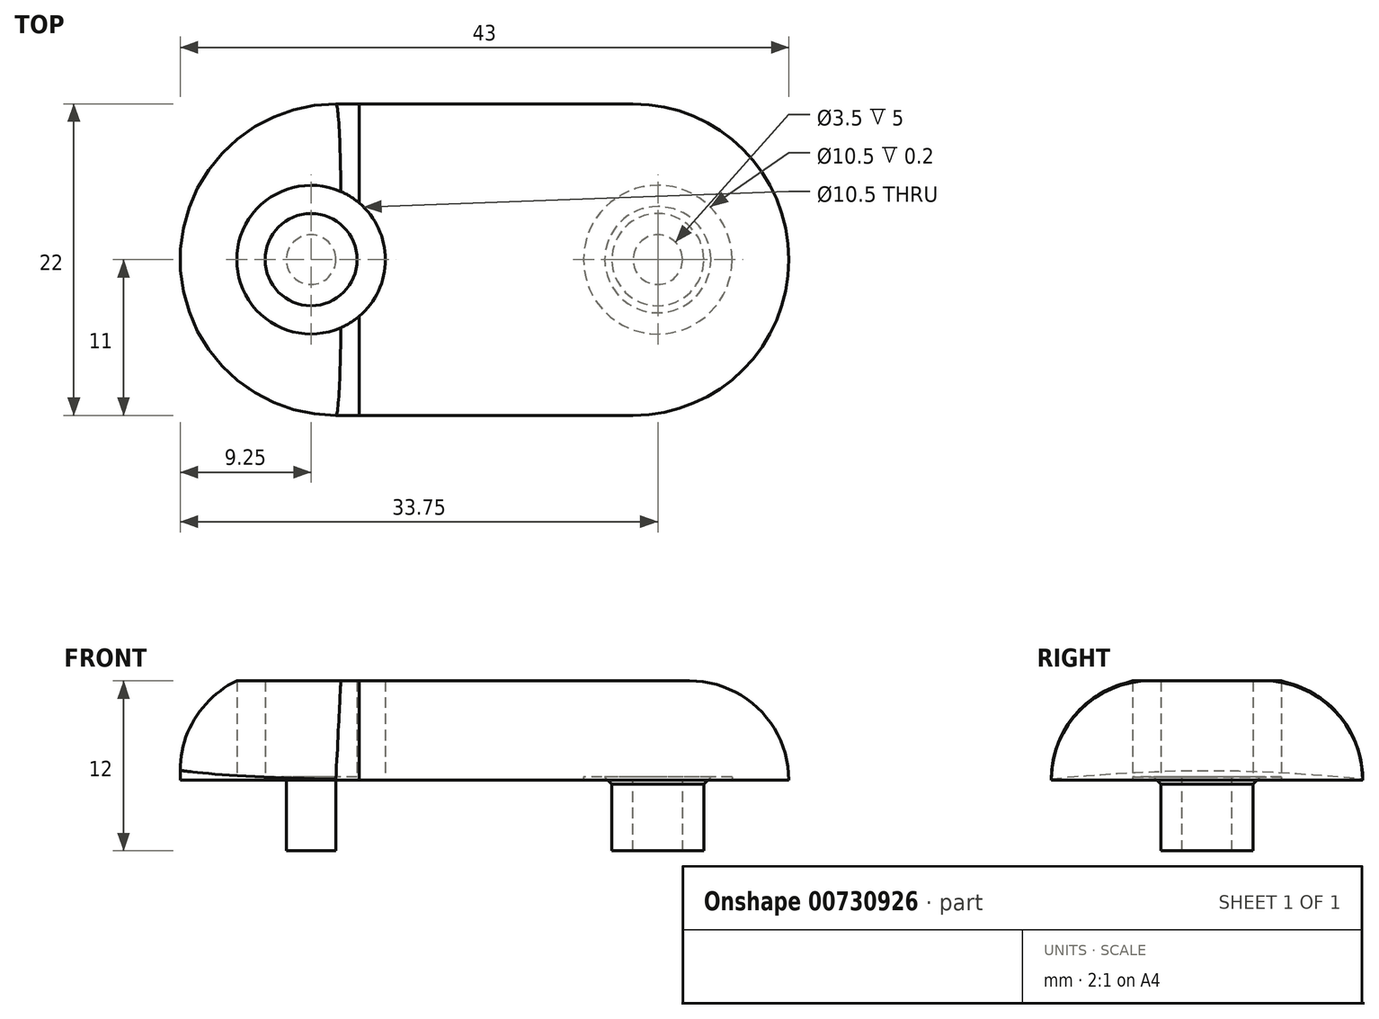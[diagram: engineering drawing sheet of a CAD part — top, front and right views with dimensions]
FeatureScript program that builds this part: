
annotation { "Feature Type Name" : "Feature", "Feature Type Description" : "" }
export const myFeature = defineFeature(function(context is Context, id is Id, definition is map)
    precondition{}
    {
        {
            var Q0;
            Q0=qCreatedBy(makeId("Top.planeOp"),FACE);
            var sketch = newSketch(context, id + "F0", { "sketchPlane" : qUnion([Q0])});
            skLineSegment(sketch, "E0", {"start": v(21.5, 0) * mm, "end": v(-21.5, 0) * mm, "construction": true});
            skLineSegment(sketch, "E1", {"start": v(0, 11) * mm, "end": v(0, -11) * mm, "construction": true});
            skLineSegment(sketch, "E2", {"start": v(-21.5, 0) * mm, "end": v(-21.5, 0) * mm});
            skLineSegment(sketch, "E3", {"start": v(-10.5, 11) * mm, "end": v(10.5, 11) * mm});
            skLineSegment(sketch, "E4", {"start": v(21.5, 0) * mm, "end": v(21.5, 0) * mm});
            skLineSegment(sketch, "E5", {"start": v(10.5, -11) * mm, "end": v(-10.5, -11) * mm});
            skPoint(sketch, "E6.visualSharp", {"position": v(-21.5, 11) * mm});
            skArc(sketch, "E6.filletArc", {"start": v(-10.5, 11) * mm, "mid": v(-18.28, 7.78) * mm, "end": v(-21.5, 0) * mm});
            skPoint(sketch, "E7.visualSharp", {"position": v(-21.5, -11) * mm});
            skArc(sketch, "E7.filletArc", {"start": v(-21.5, 0) * mm, "mid": v(-18.28, -7.78) * mm, "end": v(-10.5, -11) * mm});
            skPoint(sketch, "E8.visualSharp", {"position": v(21.5, -11) * mm});
            skArc(sketch, "E8.filletArc", {"start": v(10.5, -11) * mm, "mid": v(18.28, -7.78) * mm, "end": v(21.5, 0) * mm});
            skPoint(sketch, "E9.visualSharp", {"position": v(21.5, 11) * mm});
            skArc(sketch, "E9.filletArc", {"start": v(21.5, 0) * mm, "mid": v(18.28, 7.78) * mm, "end": v(10.5, 11) * mm});
            skCircle(sketch, "E10", {"center": v(12.25, 0) * mm, "radius": 3.25 * mm});
            skCircle(sketch, "E11.0", {"center": v(12.25, 0) * mm, "radius": 1.75 * mm});
            skCircle(sketch, "E12.MirrorC", {"center": v(-12.25, 0) * mm, "radius": 1.75 * mm});
            skCircle(sketch, "E13.MirrorC", {"center": v(-12.25, 0) * mm, "radius": 3.25 * mm});
            skCircle(sketch, "E14.0", {"center": v(12.25, 0) * mm, "radius": 5.25 * mm});
            skCircle(sketch, "E15.MirrorC", {"center": v(-12.25, 0) * mm, "radius": 5.25 * mm});
            skSolve(sketch);
        }
        {
            var Q0;
            Q0 = qSketchRegion(id + "F0", true);
            var Q1;
            Q1=makeQuery(id+"F0.imprint","IMPRINT",FACE,{"disambiguationData":[TD([[makeQuery(id+"F0.imprint","IMPRINT",EDGE,{"derivedFrom":sQuery(id+"F0.wireOp",EDGE,"E10")}),1.0]])]});
            var Q2;
            Q2=makeQuery(id+"F0.imprint","IMPRINT",FACE,{"disambiguationData":[TD([[makeQuery(id+"F0.imprint","IMPRINT",EDGE,{"derivedFrom":sQuery(id+"F0.wireOp",EDGE,"464fe94d-2eab-4d05-92af-5368927bac3c0.MirrorC")}),-1.0]])]});
            var Q3;
            Q3=makeQuery(id+"F0.imprint","IMPRINT",FACE,{"disambiguationData":[TD([[makeQuery(id+"F0.imprint","IMPRINT",EDGE,{"derivedFrom":sQuery(id+"F0.wireOp",EDGE,"E13.MirrorC")}),1.0]])]});
            var Q4;
            Q4=makeQuery(id+"F0.imprint","IMPRINT",FACE,{"disambiguationData":[TD([[makeQuery(id+"F0.imprint","IMPRINT",EDGE,{"derivedFrom":sQuery(id+"F0.wireOp",EDGE,"E12.MirrorC")}),1.0]])]});
            var Q5;
            Q5=makeQuery(id+"F0.imprint","IMPRINT",FACE,{"disambiguationData":[TD([[makeQuery(id+"F0.imprint","IMPRINT",EDGE,{"derivedFrom":sQuery(id+"F0.wireOp",EDGE,"E12.MirrorC")}),-1.0]])]});
            var Q6;
            Q6=makeQuery(id+"F0.imprint","IMPRINT",FACE,{"disambiguationData":[TD([[makeQuery(id+"F0.imprint","IMPRINT",EDGE,{"derivedFrom":sQuery(id+"F0.wireOp",EDGE,"E10")}),-1.0]])]});
            var Q7;
            Q7=makeQuery(id+"F0.imprint","IMPRINT",FACE,{"disambiguationData":[TD([[makeQuery(id+"F0.imprint","IMPRINT",EDGE,{"derivedFrom":sQuery(id+"F0.wireOp",EDGE,"E11.0")}),1.0]])]});
            extrude(context, id + "F1", {"entities" : qUnion([Q0, Q1, Q2, Q3, Q4, Q5, Q6, Q7]), "depth" : 7 * mm, "offsetDistance" : 25 * mm});
        }
        {
            var Q0;
            Q0=makeQuery(id+"F1.opExtrude","CAP_EDGE",EDGE,{"disambiguationData":[OSD([sQuery(id+"F0.wireOp",EDGE,"E3")])],"isStart":false});
            fillet(context, id + "F2", {"entities" : qUnion([Q0]), "radius" : 7 * mm, "tangentPropagation" : true, "allowEdgeOverflow" : false});
        }
        {
            var Q0;
            Q0=makeQuery(id+"F0.imprint","IMPRINT",FACE,{"disambiguationData":[TD([[makeQuery(id+"F0.imprint","IMPRINT",EDGE,{"derivedFrom":sQuery(id+"F0.wireOp",EDGE,"E10")}),1.0]])]});
            var Q1;
            Q1=makeQuery(id+"F0.imprint","IMPRINT",FACE,{"disambiguationData":[TD([[makeQuery(id+"F0.imprint","IMPRINT",EDGE,{"derivedFrom":sQuery(id+"F0.wireOp",EDGE,"E12.MirrorC")}),1.0]])]});
            extrude(context, id + "F3", {"entities" : qUnion([Q0, Q1]), "operationType" : NewBodyOperationType.ADD, "oppositeDirection" : true, "depth" : 5 * mm, "offsetDistance" : 25 * mm});
        }
        {
            var Q0;
            Q0=makeQuery(id+"F0.imprint","IMPRINT",FACE,{"disambiguationData":[TD([[makeQuery(id+"F0.imprint","IMPRINT",EDGE,{"derivedFrom":sQuery(id+"F0.wireOp",EDGE,"E13.MirrorC")}),1.0]])]});
            var Q1;
            Q1=makeQuery(id+"F0.imprint","IMPRINT",FACE,{"disambiguationData":[TD([[makeQuery(id+"F0.imprint","IMPRINT",EDGE,{"derivedFrom":sQuery(id+"F0.wireOp",EDGE,"E10")}),-1.0]])]});
            extrude(context, id + "F4", {"entities" : qUnion([Q0, Q1]), "operationType" : NewBodyOperationType.REMOVE, "depth" : 0.2 * mm, "offsetDistance" : 25 * mm});
        }
        {
            var Q0;
            Q0=makeQuery(id+"F4.boolean.opBoolean","COPY",EDGE,{"derivedFrom":makeQuery(id+"F4.opExtrude","CAP_EDGE",EDGE,{"disambiguationData":[OSD([sQuery(id+"F0.wireOp",EDGE,"E13.MirrorC")])],"isStart":false})});
            var Q1;
            Q1=makeQuery(id+"F4.boolean.opBoolean","COPY",EDGE,{"derivedFrom":makeQuery(id+"F4.opExtrude","CAP_EDGE",EDGE,{"disambiguationData":[OSD([sQuery(id+"F0.wireOp",EDGE,"E10")])],"isStart":false})});
            chamfer(context, id + "F5", {"entities" : qUnion([Q0, Q1]), "width" : 0.5 * mm, "tangentPropagation" : true});
        }
        {
            var Q0;
            Q0=makeQuery(id+"F3.opExtrude","CAP_FACE",FACE,{"disambiguationData":[OSD([sQuery(id+"F0.wireOp",EDGE,"E12.MirrorC"),sQuery(id+"F0.wireOp",EDGE,"E13.MirrorC")])],"isStart":false});
            var sketch = newSketch(context, id + "F6", { "sketchPlane" : qUnion([Q0])});
            skCircle(sketch, "E16.0", {"center": v(-12.25, 0) * mm, "radius": 2.75 * mm});
            skCircle(sketch, "E17.0", {"center": v(12.25, 0) * mm, "radius": 2.75 * mm});
            skSolve(sketch);
        }
        {
            var Q0;
            Q0=makeQuery(id+"F6.imprint","IMPRINT",FACE,{"disambiguationData":[TD([[makeQuery(id+"F6.imprint","IMPRINT",EDGE,{"derivedFrom":sQuery(id+"F6.wireOp",EDGE,"E16.0")}),1.0]])]});
            var Q1;
            Q1=makeQuery(id+"F6.imprint","IMPRINT",FACE,{"disambiguationData":[TD([[makeQuery(id+"F6.imprint","IMPRINT",EDGE,{"derivedFrom":sQuery(id+"F6.wireOp",EDGE,"E17.0")}),-1.0]])]});
            extrude(context, id + "F7", {"entities" : qUnion([Q0, Q1]), "operationType" : NewBodyOperationType.REMOVE, "oppositeDirection" : true, "depth" : 0.5 * mm, "offsetDistance" : 25 * mm});
        }
    });
